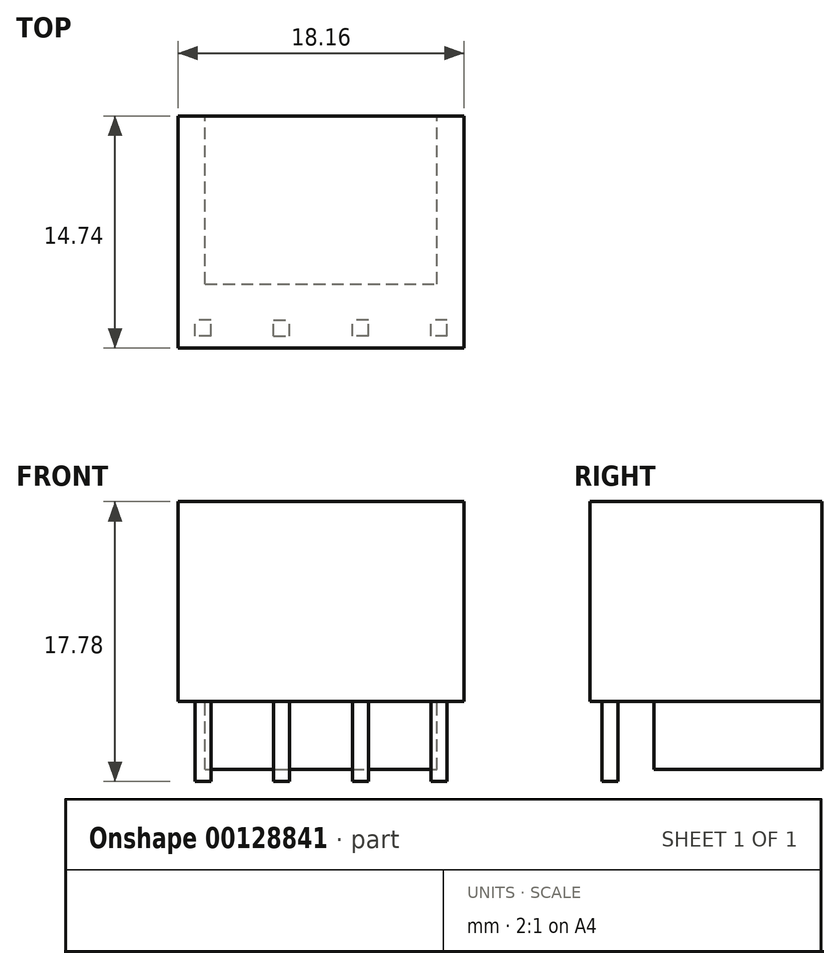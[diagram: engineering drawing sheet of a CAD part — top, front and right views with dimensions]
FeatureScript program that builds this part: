
annotation { "Feature Type Name" : "Feature", "Feature Type Description" : "" }
export const myFeature = defineFeature(function(context is Context, id is Id, definition is map)
    precondition{}
    {
        {
            var Q0;
            Q0=qCreatedBy(makeId("Top.planeOp"),FACE);
            var sketch = newSketch(context, id + "F0", { "sketchPlane" : qUnion([Q0])});
            skLineSegment(sketch, "E0.bottom", {"start": v(-9.08, -7.37) * mm, "end": v(9.08, -7.37) * mm});
            skLineSegment(sketch, "E0.top", {"start": v(-9.08, 7.37) * mm, "end": v(9.08, 7.37) * mm});
            skLineSegment(sketch, "E0.left", {"start": v(-9.08, -7.37) * mm, "end": v(-9.08, 7.37) * mm});
            skLineSegment(sketch, "E0.right", {"start": v(9.08, -7.37) * mm, "end": v(9.08, 7.37) * mm});
            skPoint(sketch, "E0.middle", {"position": v(0, 0) * mm});
            skSolve(sketch);
        }
        {
            var Q0;
            Q0 = qSketchRegion(id + "F0", true);
            extrude(context, id + "F1", {"entities" : qUnion([Q0]), "depth" : 12.7 * mm});
        }
        {
            var Q0;
            Q0=makeQuery(id+"F1.opExtrude","CAP_FACE",FACE,{"disambiguationData":[OSD([sQuery(id+"F0.wireOp",EDGE,"E0.bottom"),sQuery(id+"F0.wireOp",EDGE,"E0.top"),sQuery(id+"F0.wireOp",EDGE,"E0.left"),sQuery(id+"F0.wireOp",EDGE,"E0.right")])],"isStart":true});
            var sketch = newSketch(context, id + "F2", { "sketchPlane" : qUnion([Q0])});
            skLineSegment(sketch, "E1.bottom", {"start": v(-7.37, 3.3) * mm, "end": v(7.37, 3.3) * mm});
            skLineSegment(sketch, "E1.top", {"start": v(-7.37, -7.37) * mm, "end": v(7.37, -7.37) * mm});
            skLineSegment(sketch, "E1.left", {"start": v(-7.37, 3.3) * mm, "end": v(-7.37, -7.37) * mm});
            skLineSegment(sketch, "E1.right", {"start": v(7.37, 3.3) * mm, "end": v(7.37, -7.37) * mm});
            skSolve(sketch);
        }
        {
            var Q0;
            Q0 = qSketchRegion(id + "F2", true);
            extrude(context, id + "F3", {"entities" : qUnion([Q0]), "operationType" : NewBodyOperationType.ADD, "depth" : 4.32 * mm});
        }
        {
            var Q0;
            Q0=makeQuery(id+"F1.opExtrude","CAP_FACE",FACE,{"disambiguationData":[OSD([sQuery(id+"F0.wireOp",EDGE,"E0.bottom"),sQuery(id+"F0.wireOp",EDGE,"E0.top"),sQuery(id+"F0.wireOp",EDGE,"E0.left"),sQuery(id+"F0.wireOp",EDGE,"E0.right")])],"isStart":true});
            var sketch = newSketch(context, id + "F4", { "sketchPlane" : qUnion([Q0])});
            skLineSegment(sketch, "E2", {"start": v(-9.08, 6.1) * mm, "end": v(9.08, 6.1) * mm, "construction": true});
            skLineSegment(sketch, "E3.bottom", {"start": v(-7, 6.6) * mm, "end": v(-8, 6.6) * mm});
            skLineSegment(sketch, "E3.top", {"start": v(-7, 5.59) * mm, "end": v(-8, 5.59) * mm});
            skLineSegment(sketch, "E3.left", {"start": v(-7, 6.6) * mm, "end": v(-7, 5.59) * mm});
            skLineSegment(sketch, "E3.right", {"start": v(-8, 6.6) * mm, "end": v(-8, 5.59) * mm});
            skPoint(sketch, "E3.middle", {"position": v(-7.5, 6.1) * mm});
            skLineSegment(sketch, "E4.bottom", {"start": v(-3, 6.6) * mm, "end": v(-2, 6.6) * mm});
            skLineSegment(sketch, "E4.top", {"start": v(-3, 5.59) * mm, "end": v(-2, 5.59) * mm});
            skLineSegment(sketch, "E4.left", {"start": v(-3, 6.6) * mm, "end": v(-3, 5.59) * mm});
            skLineSegment(sketch, "E4.right", {"start": v(-2, 6.6) * mm, "end": v(-2, 5.59) * mm});
            skPoint(sketch, "E4.middle", {"position": v(-2.5, 6.1) * mm});
            skLineSegment(sketch, "E5.bottom", {"start": v(3, 6.6) * mm, "end": v(2, 6.6) * mm});
            skLineSegment(sketch, "E5.top", {"start": v(3, 5.59) * mm, "end": v(2, 5.59) * mm});
            skLineSegment(sketch, "E5.left", {"start": v(3, 6.6) * mm, "end": v(3, 5.59) * mm});
            skLineSegment(sketch, "E5.right", {"start": v(2, 6.6) * mm, "end": v(2, 5.59) * mm});
            skPoint(sketch, "E5.middle", {"position": v(2.5, 6.1) * mm});
            skLineSegment(sketch, "E6.bottom", {"start": v(8, 6.6) * mm, "end": v(7, 6.6) * mm});
            skLineSegment(sketch, "E6.top", {"start": v(8, 5.59) * mm, "end": v(7, 5.59) * mm});
            skLineSegment(sketch, "E6.left", {"start": v(8, 6.6) * mm, "end": v(8, 5.59) * mm});
            skLineSegment(sketch, "E6.right", {"start": v(7, 6.6) * mm, "end": v(7, 5.59) * mm});
            skPoint(sketch, "E6.middle", {"position": v(7.5, 6.1) * mm});
            skSolve(sketch);
        }
        {
            var Q0;
            Q0 = qSketchRegion(id + "F4", true);
            extrude(context, id + "F5", {"entities" : qUnion([Q0]), "operationType" : NewBodyOperationType.ADD, "depth" : 5.08 * mm});
        }
    });
